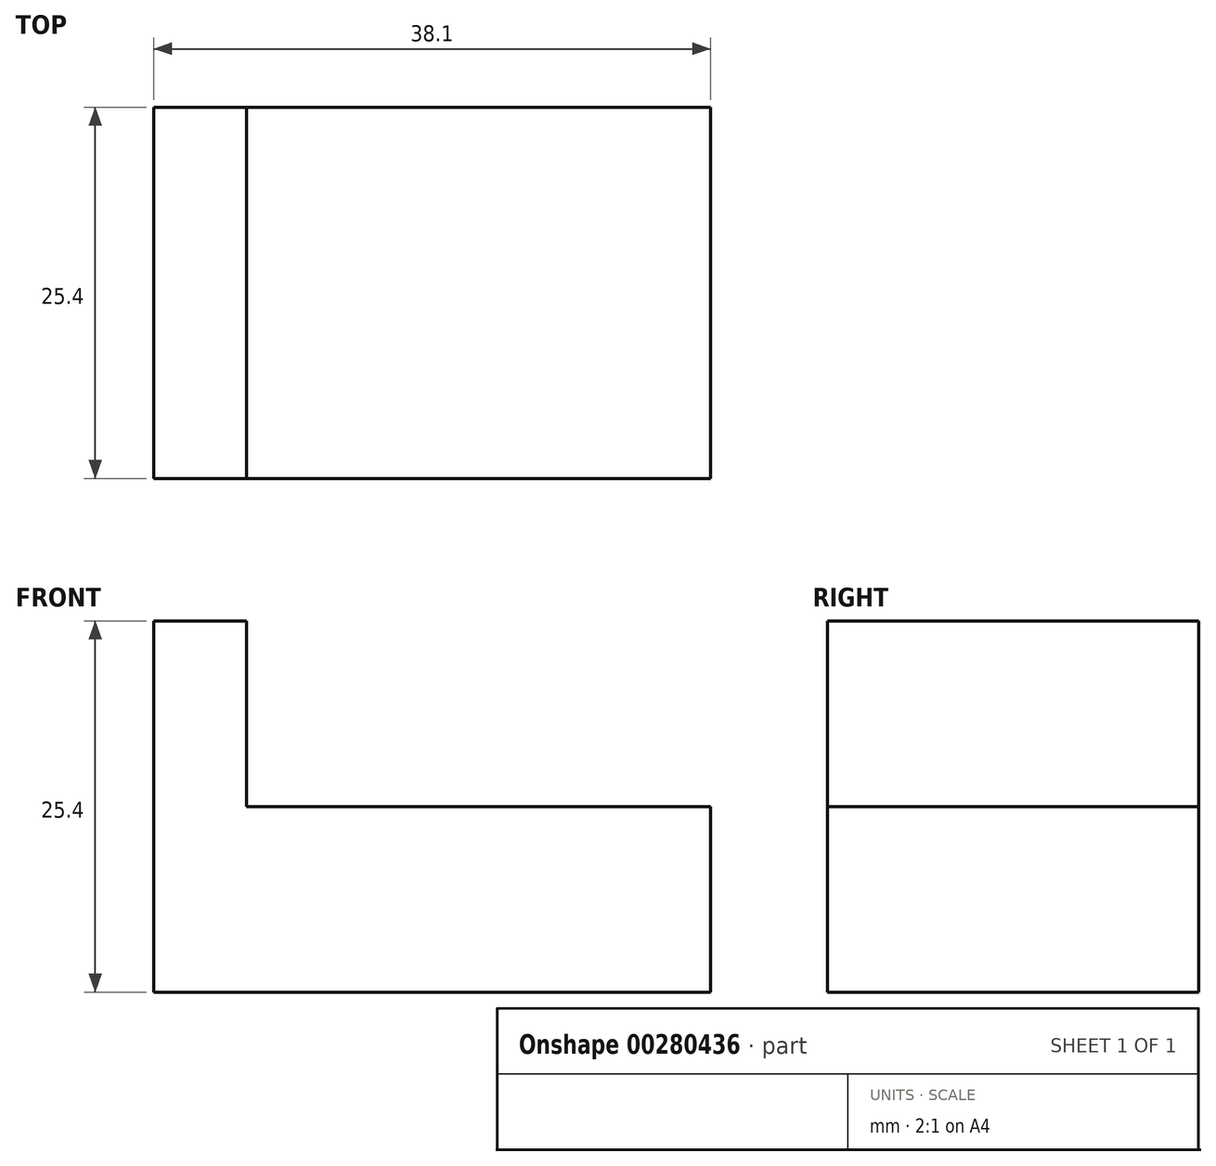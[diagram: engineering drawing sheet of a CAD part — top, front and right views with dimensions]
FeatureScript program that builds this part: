
annotation { "Feature Type Name" : "Feature", "Feature Type Description" : "" }
export const myFeature = defineFeature(function(context is Context, id is Id, definition is map)
    precondition{}
    {
        {
            var Q0;
            Q0=qCreatedBy(makeId("Front.planeOp"),FACE);
            var sketch = newSketch(context, id + "F0", { "sketchPlane" : qUnion([Q0])});
            skLineSegment(sketch, "E0.bottom", {"start": v(0, 25.4) * mm, "end": v(38.1, 25.4) * mm});
            skLineSegment(sketch, "E0.top", {"start": v(0, 0) * mm, "end": v(38.1, 0) * mm});
            skLineSegment(sketch, "E0.left", {"start": v(0, 25.4) * mm, "end": v(0, 0) * mm});
            skLineSegment(sketch, "E0.right", {"start": v(38.1, 25.4) * mm, "end": v(38.1, 0) * mm});
            skSolve(sketch);
        }
        {
            var Q0;
            Q0=makeQuery(id+"F0.imprint","IMPRINT",FACE,{"disambiguationData":[TD([[makeQuery(id+"F0.imprint","IMPRINT",EDGE,{"derivedFrom":sQuery(id+"F0.wireOp",EDGE,"E0.bottom")}),-1.0]])]});
            extrude(context, id + "F1", {"entities" : qUnion([Q0]), "depth" : 25.4 * mm});
        }
        {
            var Q0;
            Q0=qCreatedBy(makeId("Front.planeOp"),FACE);
            var sketch = newSketch(context, id + "F2", { "sketchPlane" : qUnion([Q0])});
            skLineSegment(sketch, "E1.bottom", {"start": v(6.35, 25.4) * mm, "end": v(38.1, 25.4) * mm});
            skLineSegment(sketch, "E1.top", {"start": v(6.35, 12.7) * mm, "end": v(38.1, 12.7) * mm});
            skLineSegment(sketch, "E1.left", {"start": v(6.35, 25.4) * mm, "end": v(6.35, 12.7) * mm});
            skLineSegment(sketch, "E1.right", {"start": v(38.1, 25.4) * mm, "end": v(38.1, 12.7) * mm});
            skSolve(sketch);
        }
        {
            var Q0;
            Q0 = qSketchRegion(id + "F2", true);
            extrude(context, id + "F3", {"entities" : qUnion([Q0]), "operationType" : NewBodyOperationType.REMOVE, "endBound" : BoundingType.SYMMETRIC, "depth" : 75.7 * mm});
        }
    });
